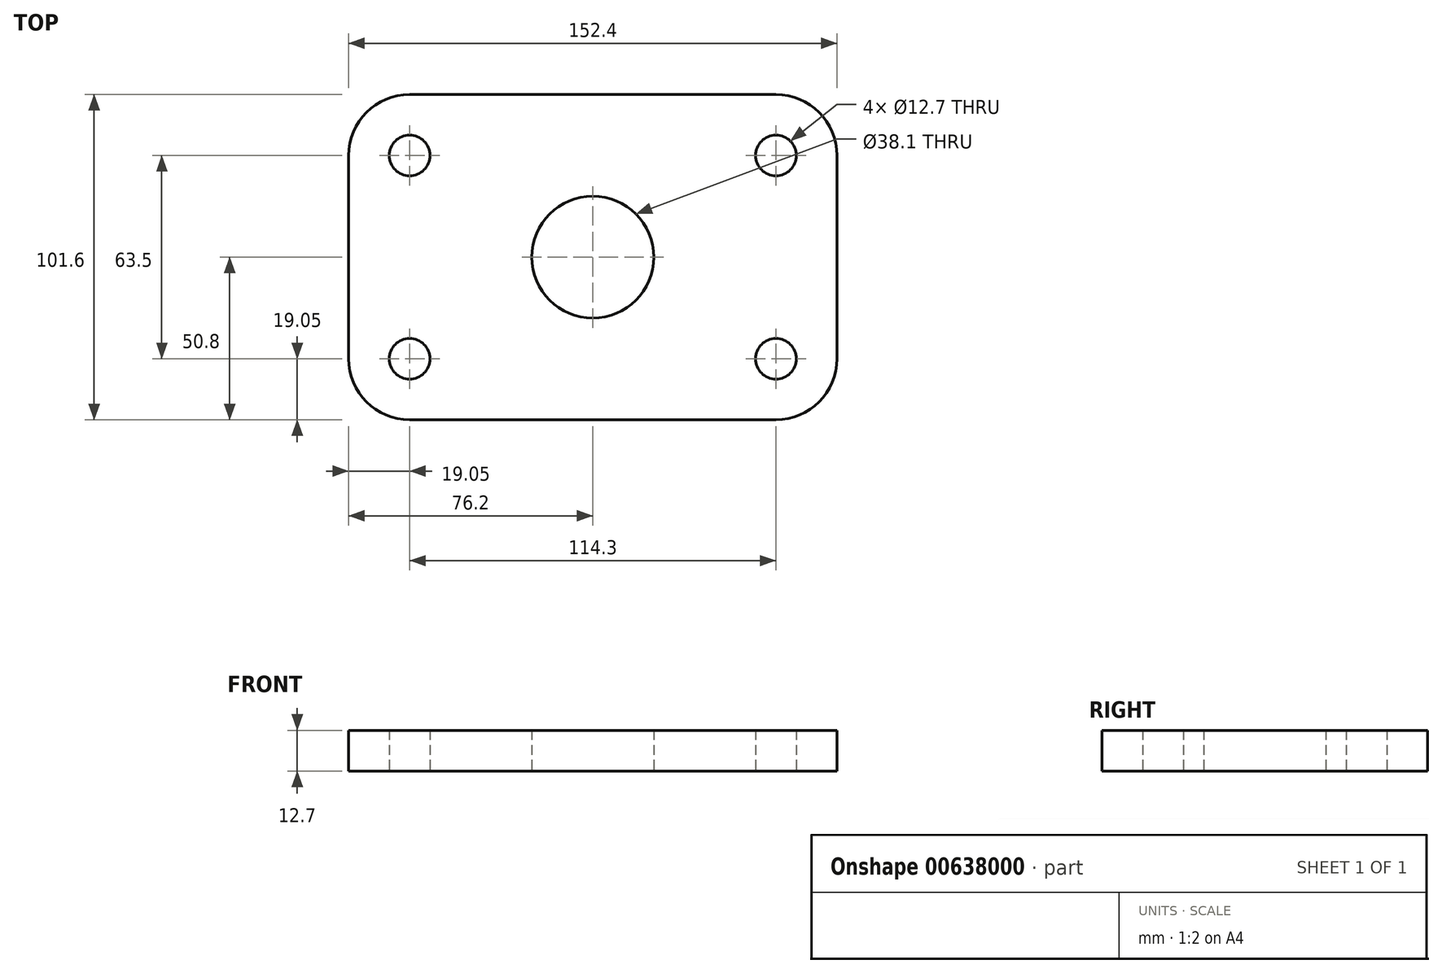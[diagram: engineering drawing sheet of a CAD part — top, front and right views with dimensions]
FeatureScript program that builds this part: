
annotation { "Feature Type Name" : "Feature", "Feature Type Description" : "" }
export const myFeature = defineFeature(function(context is Context, id is Id, definition is map)
    precondition{}
    {
        {
            var Q0;
            Q0=qCreatedBy(makeId("Top.planeOp"),FACE);
            var sketch = newSketch(context, id + "F0", { "sketchPlane" : qUnion([Q0])});
            skLineSegment(sketch, "E0.bottom", {"start": v(57.15, 50.8) * mm, "end": v(-57.15, 50.8) * mm});
            skLineSegment(sketch, "E0.top", {"start": v(57.15, -50.8) * mm, "end": v(-57.15, -50.8) * mm});
            skLineSegment(sketch, "E0.left", {"start": v(76.2, 31.75) * mm, "end": v(76.2, -31.75) * mm});
            skLineSegment(sketch, "E0.right", {"start": v(-76.2, 31.75) * mm, "end": v(-76.2, -31.75) * mm});
            skPoint(sketch, "E0.middle", {"position": v(0, 0) * mm});
            skPoint(sketch, "E1.visualSharp", {"position": v(-76.2, 50.8) * mm});
            skArc(sketch, "E1.filletArc", {"start": v(-57.15, 50.8) * mm, "mid": v(-70.62, 45.22) * mm, "end": v(-76.2, 31.75) * mm});
            skPoint(sketch, "E2.visualSharp", {"position": v(-76.2, -50.8) * mm});
            skArc(sketch, "E2.filletArc", {"start": v(-76.2, -31.75) * mm, "mid": v(-70.62, -45.22) * mm, "end": v(-57.15, -50.8) * mm});
            skPoint(sketch, "E3.visualSharp", {"position": v(76.2, -50.8) * mm});
            skArc(sketch, "E3.filletArc", {"start": v(57.15, -50.8) * mm, "mid": v(70.62, -45.22) * mm, "end": v(76.2, -31.75) * mm});
            skPoint(sketch, "E4.visualSharp", {"position": v(76.2, 50.8) * mm});
            skArc(sketch, "E4.filletArc", {"start": v(76.2, 31.75) * mm, "mid": v(70.62, 45.22) * mm, "end": v(57.15, 50.8) * mm});
            skCircle(sketch, "E5", {"center": v(0, 0) * mm, "radius": 19.05 * mm});
            skCircle(sketch, "E6", {"center": v(-57.15, -31.75) * mm, "radius": 6.35 * mm});
            skCircle(sketch, "E7", {"center": v(57.15, -31.75) * mm, "radius": 6.35 * mm});
            skCircle(sketch, "E8", {"center": v(57.15, 31.75) * mm, "radius": 6.35 * mm});
            skCircle(sketch, "E9", {"center": v(-57.15, 31.75) * mm, "radius": 6.35 * mm});
            skSolve(sketch);
        }
        {
            var Q0;
            Q0=makeQuery(id+"F0.imprint","IMPRINT",FACE,{"disambiguationData":[TD([[makeQuery(id+"F0.imprint","IMPRINT",EDGE,{"derivedFrom":sQuery(id+"F0.wireOp",EDGE,"E0.bottom")}),1.0]])]});
            var Q1;
            Q1=makeQuery(id+"F0.imprint","IMPRINT",FACE,{"disambiguationData":[TD([[makeQuery(id+"F0.imprint","IMPRINT",EDGE,{"derivedFrom":sQuery(id+"F0.wireOp",EDGE,"MfVX1maW-GLGG-pnTj-bhLn-0UECvQnALfZw")}),1.0]])]});
            extrude(context, id + "F1", {"entities" : qUnion([Q0, Q1]), "depth" : 12.7 * mm, "offsetDistance" : 25.4 * mm});
        }
    });
